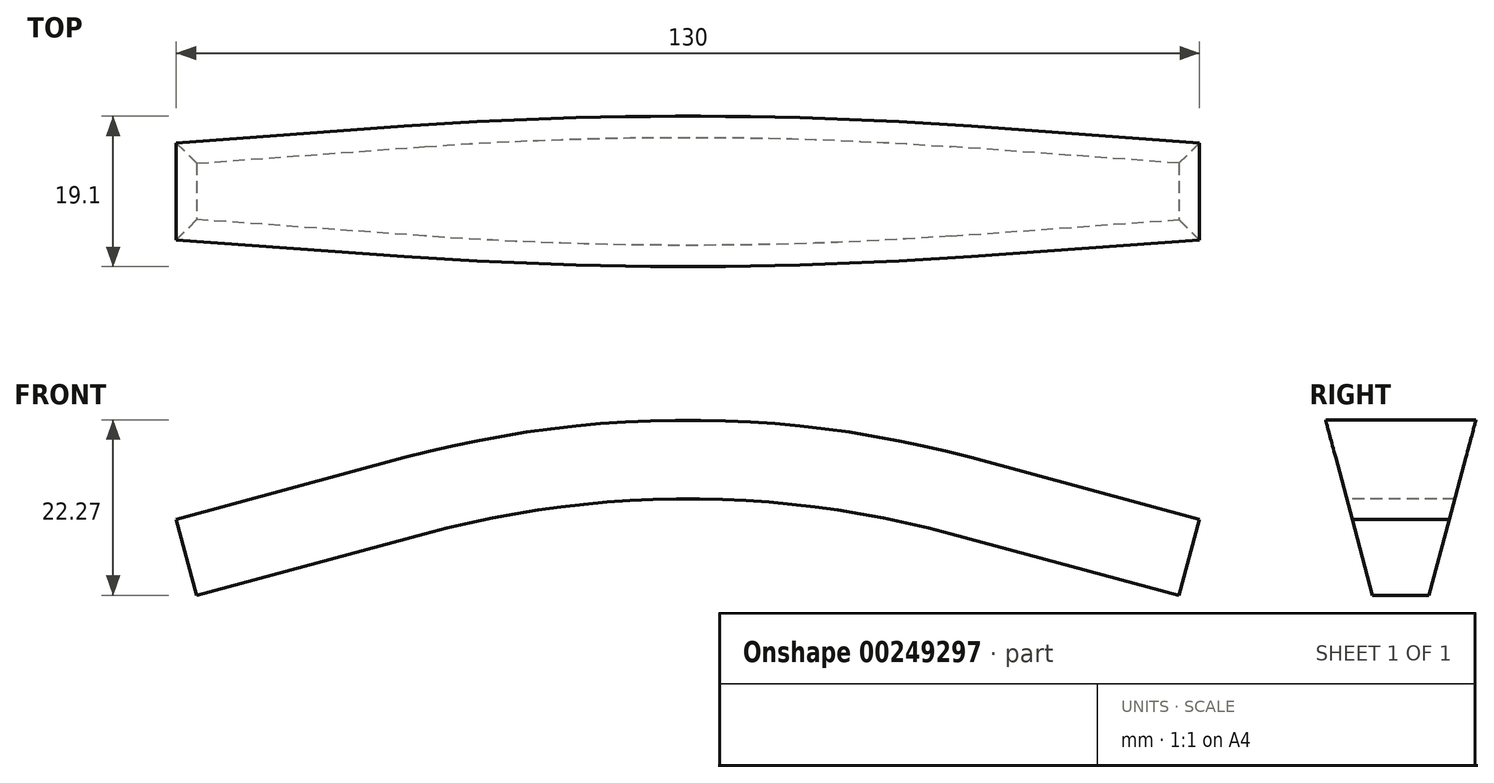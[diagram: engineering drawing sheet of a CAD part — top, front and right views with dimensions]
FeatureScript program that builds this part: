
annotation { "Feature Type Name" : "Feature", "Feature Type Description" : "" }
export const myFeature = defineFeature(function(context is Context, id is Id, definition is map)
    precondition{}
    {
        {
            var Q0;
            Q0=qCreatedBy(makeId("Front.planeOp"),FACE);
            var sketch = newSketch(context, id + "F0", { "sketchPlane" : qUnion([Q0])});
            skLineSegment(sketch, "E0", {"start": v(32.9, 19.26) * mm, "end": v(61.87, 11.43) * mm});
            skLineSegment(sketch, "E1", {"start": v(61.87, 11.43) * mm, "end": v(65, 23.02) * mm});
            skLineSegment(sketch, "E2", {"start": v(65, 23.02) * mm, "end": v(36.04, 30.84) * mm});
            skArc(sketch, "E3", {"start": v(32.9, 19.26) * mm, "mid": v(0, 23.63) * mm, "end": v(-32.9, 19.26) * mm});
            skArc(sketch, "E4", {"start": v(36.04, 30.84) * mm, "mid": v(0, 35.63) * mm, "end": v(-36.04, 30.84) * mm});
            skLineSegment(sketch, "E5", {"start": v(-32.9, 19.26) * mm, "end": v(-61.87, 11.43) * mm});
            skLineSegment(sketch, "E6", {"start": v(-36.04, 30.84) * mm, "end": v(-65, 23.02) * mm});
            skLineSegment(sketch, "E7", {"start": v(-61.87, 11.43) * mm, "end": v(-65, 23.02) * mm});
            skSolve(sketch);
        }
        {
            var Q0;
            Q0=makeQuery(id+"F0.imprint","IMPRINT",FACE,{"disambiguationData":[TD([[makeQuery(id+"F0.imprint","IMPRINT",EDGE,{"derivedFrom":sQuery(id+"F0.wireOp",EDGE,"E0")}),1.0]])]});
            extrude(context, id + "F1", {"entities" : qUnion([Q0]), "depth" : 30 * mm, "offsetDistance" : 25 * mm, "symmetric" : true});
        }
        {
            var Q0;
            Q0=qCreatedBy(makeId("Right.planeOp"),FACE);
            var sketch = newSketch(context, id + "F2", { "sketchPlane" : qUnion([Q0])});
            skLineSegment(sketch, "E8", {"start": v(0, 0) * mm, "end": v(-17, 63.44) * mm, "construction": true});
            skLineSegment(sketch, "E9", {"start": v(-17, 63.44) * mm, "end": v(-17, 0) * mm});
            skLineSegment(sketch, "E10", {"start": v(-17, 0) * mm, "end": v(0, 0) * mm});
            skLineSegment(sketch, "E11", {"start": v(0, 0) * mm, "end": v(17, 63.44) * mm, "construction": true});
            skLineSegment(sketch, "E12", {"start": v(17, 63.44) * mm, "end": v(17, 0) * mm});
            skLineSegment(sketch, "E13", {"start": v(17, 0) * mm, "end": v(0, 0) * mm});
            skLineSegment(sketch, "E14", {"start": v(-17, 63.44) * mm, "end": v(-1.88, 7) * mm});
            skLineSegment(sketch, "E15", {"start": v(-1.88, 7) * mm, "end": v(1.88, 7) * mm});
            skLineSegment(sketch, "E16", {"start": v(1.88, 7) * mm, "end": v(17, 63.44) * mm});
            skSolve(sketch);
        }
        {
            var Q0;
            Q0=makeQuery(id+"F2.imprint","IMPRINT",FACE,{"disambiguationData":[TD([[makeQuery(id+"F2.imprint","IMPRINT",EDGE,{"derivedFrom":sQuery(id+"F2.wireOp",EDGE,"E9")}),1.0]])]});
            extrude(context, id + "F3", {"entities" : qUnion([Q0]), "operationType" : NewBodyOperationType.REMOVE, "oppositeDirection" : true, "depth" : 200 * mm, "offsetDistance" : 25 * mm, "symmetric" : true});
        }
        {
            var Q0;
            Q0=qCreatedBy(makeId("Front.planeOp"),FACE);
            var sketch = newSketch(context, id + "F4", { "sketchPlane" : qUnion([Q0])});
            skArc(sketch, "E17.0", {"start": v(36.04, 30.84) * mm, "mid": v(0, 35.63) * mm, "end": v(-36.04, 30.84) * mm});
            skLineSegment(sketch, "E18.0", {"start": v(-36.04, 30.84) * mm, "end": v(-65, 23.02) * mm});
            skLineSegment(sketch, "E19.0", {"start": v(65, 23.02) * mm, "end": v(36.04, 30.84) * mm});
            skArc(sketch, "E20.0", {"start": v(35.52, 28.91) * mm, "mid": v(0, 33.63) * mm, "end": v(-35.52, 28.91) * mm});
            skLineSegment(sketch, "E21", {"start": v(-35.52, 28.91) * mm, "end": v(-64.48, 21.09) * mm});
            skLineSegment(sketch, "E22", {"start": v(35.52, 28.91) * mm, "end": v(64.48, 21.09) * mm});
            skLineSegment(sketch, "E23", {"start": v(65, 23.02) * mm, "end": v(64.48, 21.09) * mm});
            skLineSegment(sketch, "E24", {"start": v(-65, 23.02) * mm, "end": v(-64.48, 21.09) * mm});
            skArc(sketch, "E25.0", {"start": v(33.43, 21.2) * mm, "mid": v(0, 25.63) * mm, "end": v(-33.43, 21.2) * mm});
            skLineSegment(sketch, "E26.0", {"start": v(-28.77, 22.45) * mm, "end": v(-62.4, 13.36) * mm});
            skLineSegment(sketch, "E27.0", {"start": v(28.77, 22.45) * mm, "end": v(62.4, 13.36) * mm});
            skArc(sketch, "E28.0", {"start": v(32.9, 19.26) * mm, "mid": v(0, 23.63) * mm, "end": v(-32.9, 19.26) * mm});
            skLineSegment(sketch, "E29.0", {"start": v(-32.9, 19.26) * mm, "end": v(-61.87, 11.43) * mm});
            skLineSegment(sketch, "E30.0", {"start": v(32.9, 19.26) * mm, "end": v(61.87, 11.43) * mm});
            skLineSegment(sketch, "E31", {"start": v(-62.4, 13.36) * mm, "end": v(-61.87, 11.43) * mm});
            skLineSegment(sketch, "E32", {"start": v(62.4, 13.36) * mm, "end": v(61.87, 11.43) * mm});
            skSolve(sketch);
        }
        {
            var Q0;
            Q0=makeQuery(id+"F4.imprint","IMPRINT",FACE,{"disambiguationData":[TD([[makeQuery(id+"F4.imprint","IMPRINT",EDGE,{"derivedFrom":sQuery(id+"F4.wireOp",EDGE,"E25.0")}),1.0]])]});
            extrude(context, id + "F5", {"entities" : qUnion([Q0]), "operationType" : NewBodyOperationType.REMOVE, "oppositeDirection" : true, "depth" : 50 * mm, "offsetDistance" : 25 * mm, "symmetric" : true});
        }
    });
